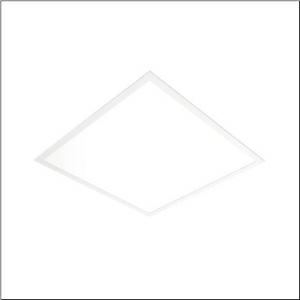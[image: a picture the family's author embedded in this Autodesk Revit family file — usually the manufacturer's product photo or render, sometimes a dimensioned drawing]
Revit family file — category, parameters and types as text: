
# Revit family: apollon_r__41_51mh11w72422_84d9
name_source: partatom
category: Lighting Fixtures
units: mm (PartAtom-declared; Revit-internal decimal feet)

## family parameters
Cut with Voids When Loaded = No
Host = Face
Light Source = No
Part Type = Normal
Room Calculation Point = No
Round Connector Dimension = Use Diameter
Shared = No

## types (1)
- Apollon® 41 (1 x LED, 3700 lm, 35 W, 4000K)
    Apparent Load = 35 VA
    CIE Flux Codes = 62 87 97 100 100
    Color Rendering = 80
    Color Temperature = 4000K
    Default Elevation = 1800 mm
    Description = Apollon® 41, office luminaire, primary optical cover: prismatic diffuser, of PS, light emission: direct distribution, primary light characteristic: symmetric, installation type: lay-in mounting, LED rated luminous flux: 3.700 lm, light colour: 840, colour temperature: 4000K, control gear: ECG, with terminal, 3-pole, mains connection: 220..240V, AC, 50/60Hz, rated input power: 35W, housing, of aluminium section, traffic white (RAL 9016), module: M625, length: 622 mm, width: 622 mm, height: 30mm, housing upper side, of sheet steel, protection rating (complete): IP20, protection rating (lamp compartment, on room side): IP40, insulation class (complete): insulation class II (safety insulation), certification: CE, ENEC, permissible ambient temperature for indoor applications: -20..+40°C, packaging unit: 1 piece
    Height = 0 mm  [stored 0 ft]
    Lamp = 1 x LED
    Lamp Light Flux = 3700 lm
    Lamp Power = 35 W
    Lamp count = 1
    Length = 620 mm
    Luminous efficacy = 106 lm/W
    Manufacturer = Siteco
    ModVariant = No
    Model = 51MH11W72422
    Mounting Place = Ceiling
    Mounting Type = Recessed
    Number of Poles = 1
    OnlyDefault = Yes
    Power Factor = 1
    Product Name = Apollon® 41
    Product group = office luminaire | ceiling recessed
    ProductGroupID = 400
    Protection Class = Protection class II
    Protection Degree = IP 20
    RLX_Detail_Level = 1
    RlxData = <blob elided: 14857 chars, md5=38ac9ea7>
    Socket = socket
    Standby Power = 0 W
    System Light Flux = 3700 lm
    System Power = 35 W
    Type Comments = Product without accessories
    Type Image = l_1003755.jpg
    URL = http://relux.com
    VarID = ---
    Voltage = 0 V
    Weight = 0.00 kg
    Width = 620 mm

note: [stored X ft] marks values corroborated as IEEE doubles in the binary element streams (Revit-internal decimal feet)

## geometry (parser evidence)
native form markers: Sweep x10
no freeform markers — native parametric forms only
